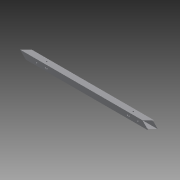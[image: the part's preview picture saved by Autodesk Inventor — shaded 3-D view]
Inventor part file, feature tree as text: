
AUTODESK INVENTOR PART (.ipt)
format: ipt  version: 2015 SP1 (Build 190203100, 203)  size: 133,120 bytes
history: native  units: in
note: dims shown in document units (in); Inventor stores cm internally (conversion verified against a paired STEP export)
features: sketch x4, extrude x2, hole x2
ambient origin geometry x8: Origin, YZ Plane, XZ Plane, XY Plane, X Axis, Y Axis, Z Axis, Center Point
bodies: Solid1 (feature_tree)
feature tree (8):
  extrude  "Extrusion1"  Depth=1.0in
  hole  "Hole2"  [1 undecoded]
  extrude  "Extrusion2"  Depth=0.125in
  hole  "Hole5"  [1 undecoded]
  sketch  "Sketch1"  dims[d0=1.0in d1=1.0in]
  sketch  "Sketch3"  dims[d2=0.75in d3=0.75in]
  sketch  "Sketch6"  dims[d4=0.125in d5=0.125in]
  sketch  "Sketch7"  dims[d6=27.0in d7=0.0in d23=1.5in d24=0.5in d25=0.5in d26=0.5in d27=4.875in d28=6.375in d29=0.5in d30=0.5in d31=0.5in d32=1.5in d33=4.875in d34=6.375in d35=0.25in d36=0.75in d37=0.375in d38=0.25in d39=0.5635in d40=1.0in d41=0.8108in d66=0.25in d67=0.25in d68=0.5in d69=0.25in d70=0.25in d71=0.5in d72=1.0in d73=0.0in d74=0.5in d75=0.5in d76=20.875in d77=6.125in d78=0.1875in d79=0.75in d80=0.375in d81=0.25in d82=0.5635in d83=1.0in d84=0.8108in]
note: 2 required parameter values undecoded (feature->parameter linkage not recoverable at this tier; creation-order binding heuristic only, values carry confidence <= 0.55)
